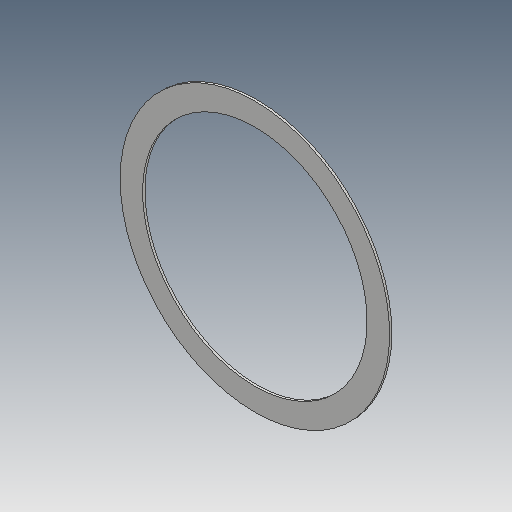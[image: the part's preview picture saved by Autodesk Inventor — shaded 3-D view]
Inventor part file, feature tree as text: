
AUTODESK INVENTOR PART (.ipt)
format: ipt  version: 2018 (Build 220112000, 112)  size: 80,384 bytes
history: native  units: mm
features: revolve x1
ambient origin geometry x8: Origin, YZ Plane, XZ Plane, XY Plane, X Axis, Y Axis, Z Axis, Center Point
bodies: Volumenkörper1 (feature_tree)
feature tree (1):
  revolve  "Revolve1"  [1 undecoded]
note: 1 required parameter value undecoded (feature->parameter linkage not recoverable at this tier; creation-order binding heuristic only, values carry confidence <= 0.55)
